# Revit family: 031455
name_source: partatom
category: Sanitärinstallationen
revit_build: Autodesk Revit 2014 (Build: 20130308_1515(x64)
units: mm (PartAtom-declared; Revit-internal decimal feet)

## types (1)
- 031455
    Abwasserrohrverbindung = Nein
    Aufbau Waschtisch = 30 mm  [stored 0.0984252 ft]
    Baugruppenkennzeichen = D2010400
    Behindertengerecht / ADA Compliant = Ja
    Familie von / Family made By = http://bytesandbuilding.de
    HW-Verbindung = Nein
    Hersteller = Duravit
    KW-Verbindung = Nein
    LEED Credit = 0
    Lüftungsverbindung = Nein
    Material Chrom = Stahl, verchromt
    Material Keramik = Duravit Keramik
    Material Platte/ Material Surface = Sperrholz, Verkleidung
    Modell = 031455
    Modellbezeichnung / Modeldescription = Halbeinbau-WT 550mm Vero Weiss / Semi-recessed washbasin 550mm Vero
    Produktseite / Product URL = http://www.pro.duravit.com
    URL = http://www.duravit.de

note: [stored X ft] marks values corroborated as IEEE doubles in the binary element streams (Revit-internal decimal feet)
